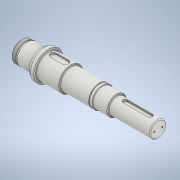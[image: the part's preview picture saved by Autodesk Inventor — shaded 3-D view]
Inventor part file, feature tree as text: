
AUTODESK INVENTOR PART (.ipt)
format: ipt  version: 2020 (Build 240168000, 168)  size: 290,304 bytes
history: native  units: mm
features: sketch x8, extrude x6, other x4, plane x3, revolve x1, hole x1, thread x1, chamfer x1, fillet x1, projected_geometry x1
ambient origin geometry x6: Origin, XZ Plane, XY Plane, X Axis, Y Axis, Z Axis
bodies: 实体1 (feature_tree)
feature tree (27):
  revolve  "旋转1"  [1 undecoded]
  other  "键槽1"
  plane  "工作平面1"
  extrude  "拉伸1"  Depth=90.0mm
  plane  "工作平面2"
  hole  "孔1"  [1 undecoded]
  extrude  "拉伸3"  TaperAngle=0.0deg  [1 undecoded]
  extrude  "拉伸4"  [1 undecoded]
  sketch  "草图8"  dims[d10=60.0mm d11=-11.0mm]
  extrude  "拉伸5"  Depth=62.0mm TaperAngle=0.0deg
  thread  "螺纹1"  [1 undecoded]
  plane  "工作平面3"
  extrude  "拉伸6"  Depth=18.0mm TaperAngle=0.0deg
  chamfer  "倒角1"  Distance=5.0mm
  extrude  "拉伸7"  Depth=64.0mm
  fillet  "圆角1"  Radius=13.0mm
  other  "起始平面"
  other  "主草图"
  other  "iFeature3:1"
  sketch  "草图3"  dims[d0=0.0mm d1=0.0mm d2=0.0mm d3=65.0mm]
  sketch  "草图4"  dims[d4=78.0mm d5=90.0mm]
  projected_geometry  "投影回路1"
  sketch  "草图6"  dims[d6=75.0mm d7=65.0mm]
  sketch  "草图7"  dims[d8=50.0mm d9=0.0mm]
  sketch  "草图9"  dims[d12=62.0mm d13=2.5mm d14=0.0mm d15=25.0mm]
  sketch  "草图11"  dims[d16=4.917mm d17=18.0mm d18=20.0mm d19=2.0mm d20=90.0deg d21=18.0mm d22=20.594885mm d25=18.0mm d26=0.0mm]
  sketch  "草图12"  dims[d27=61.0mm d28=5.0mm d29=0.0mm d30=64.0mm d31=13.0mm d32=0.0mm d33=13.0mm d34=0.0mm d39=7.0mm d40=76.0mm d41=65.0mm d42=5.5mm d43=0.0mm d44=2.5mm d45=2.0mm d46=45.0deg d47=1.6mm d48=0.5mm d49=0.0mm d50=0.5mm d51=0.872665mm]
note: 5 required parameter values undecoded (feature->parameter linkage not recoverable at this tier; creation-order binding heuristic only, values carry confidence <= 0.55)